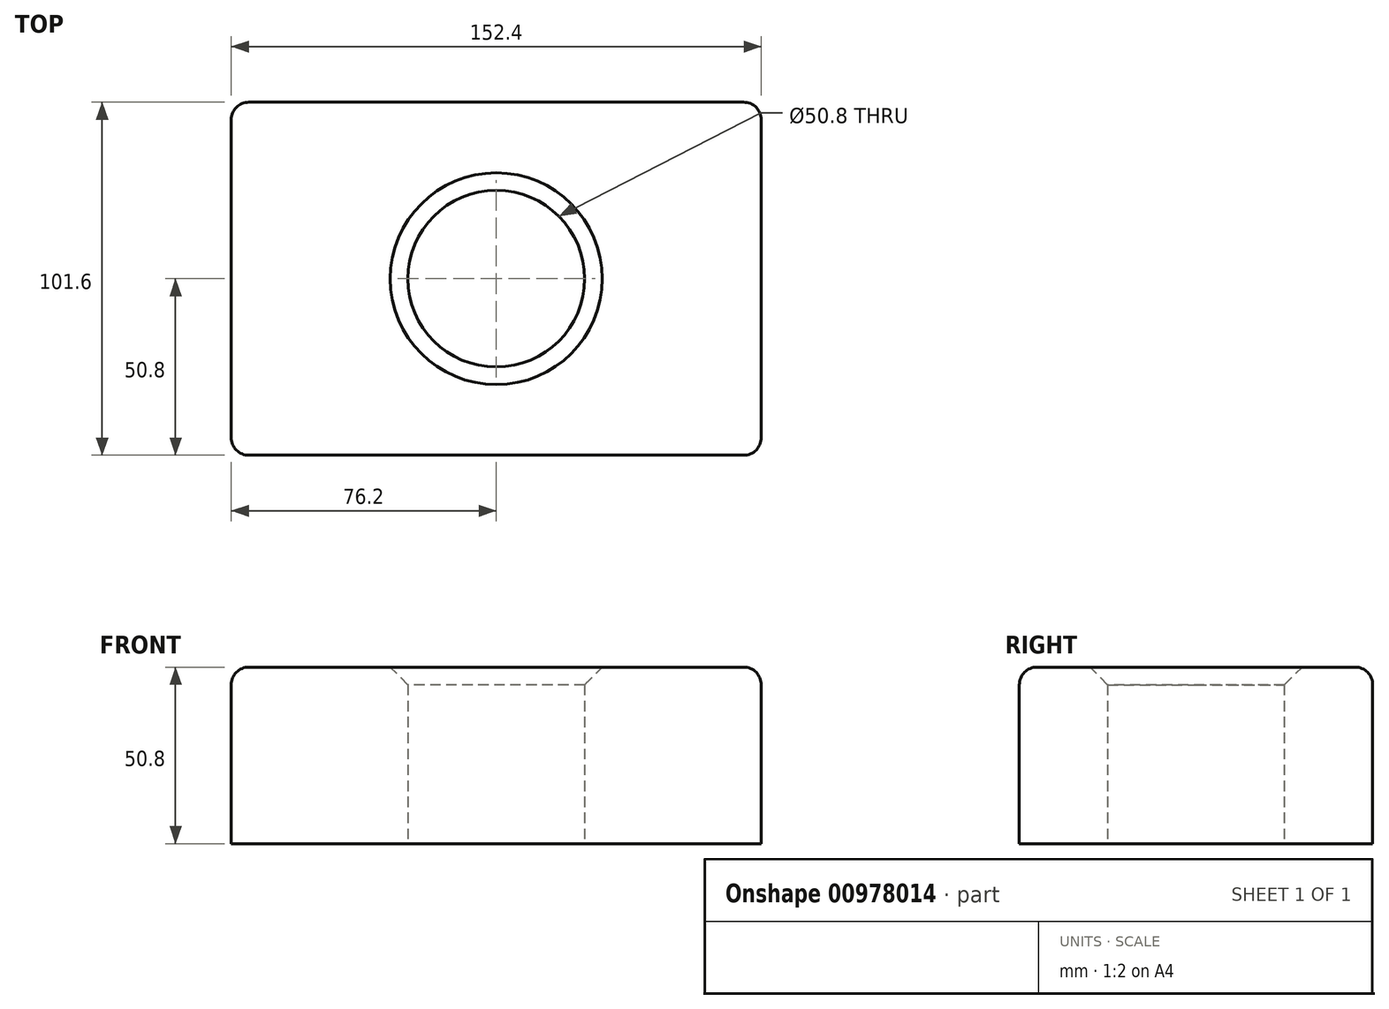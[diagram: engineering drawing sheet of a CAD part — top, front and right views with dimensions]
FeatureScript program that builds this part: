
annotation { "Feature Type Name" : "Feature", "Feature Type Description" : "" }
export const myFeature = defineFeature(function(context is Context, id is Id, definition is map)
    precondition{}
    {
        {
            var Q0;
            Q0=qCreatedBy(makeId("Top.planeOp"),FACE);
            var sketch = newSketch(context, id + "F0", { "sketchPlane" : qUnion([Q0])});
            skLineSegment(sketch, "E0.bottom", {"start": v(-76.2, 50.8) * mm, "end": v(76.2, 50.8) * mm});
            skLineSegment(sketch, "E0.top", {"start": v(-76.2, -50.8) * mm, "end": v(76.2, -50.8) * mm});
            skLineSegment(sketch, "E0.left", {"start": v(-76.2, 50.8) * mm, "end": v(-76.2, -50.8) * mm});
            skLineSegment(sketch, "E0.right", {"start": v(76.2, 50.8) * mm, "end": v(76.2, -50.8) * mm});
            skPoint(sketch, "E0.middle", {"position": v(0, 0) * mm});
            skCircle(sketch, "E1", {"center": v(0, 0) * mm, "radius": 25.4 * mm});
            skSolve(sketch);
        }
        {
            var Q0;
            Q0=makeQuery(id+"F0.imprint","IMPRINT",FACE,{"disambiguationData":[TD([[makeQuery(id+"F0.imprint","IMPRINT",EDGE,{"derivedFrom":sQuery(id+"F0.wireOp",EDGE,"E0.bottom")}),-1.0]])]});
            extrude(context, id + "F1", {"entities" : qUnion([Q0]), "depth" : 50.8 * mm, "offsetDistance" : 25.4 * mm});
        }
        {
            var Q0;
            Q0=makeQuery(id+"F1.opExtrude","CAP_EDGE",EDGE,{"disambiguationData":[OSD([sQuery(id+"F0.wireOp",EDGE,"E0.top")])],"isStart":false});
            fillet(context, id + "F2", {"entities" : qUnion([Q0]), "radius" : 5.08 * mm, "tangentPropagation" : true, "allowEdgeOverflow" : false});
        }
        {
            var Q0;
            Q0=makeQuery(id+"F1.opExtrude","CAP_EDGE",EDGE,{"disambiguationData":[OSD([sQuery(id+"F0.wireOp",EDGE,"E0.right")])],"isStart":false});
            fillet(context, id + "F3", {"entities" : qUnion([Q0]), "radius" : 5.08 * mm, "tangentPropagation" : true, "allowEdgeOverflow" : false});
        }
        {
            var Q0;
            Q0=makeQuery(id+"F1.opExtrude","CAP_EDGE",EDGE,{"disambiguationData":[OSD([sQuery(id+"F0.wireOp",EDGE,"E0.left")])],"isStart":false});
            fillet(context, id + "F4", {"entities" : qUnion([Q0]), "radius" : 5.08 * mm, "tangentPropagation" : true, "allowEdgeOverflow" : false});
        }
        {
            var Q0;
            {var subQ0=sQuery(id+"F0.wireOp",EDGE,"E0.left");Q0=makeQuery(id+"F4.opFillet","BLEND_EDGE",EDGE,{"blendedFrom":[makeQuery(id+"F1.opExtrude","CAP_EDGE",EDGE,{"disambiguationData":[OSD([subQ0])],"isStart":false}),makeQuery(id+"F1.opExtrude","CAP_FACE",FACE,{"disambiguationData":[OSD([sQuery(id+"F0.wireOp",EDGE,"E0.bottom"),sQuery(id+"F0.wireOp",EDGE,"E0.top"),subQ0,sQuery(id+"F0.wireOp",EDGE,"E0.right"),sQuery(id+"F0.wireOp",EDGE,"E1")])],"isStart":false})],"blendedInto":[makeQuery(id+"F1.opExtrude","CAP_FACE",FACE,{"disambiguationData":[OSD([sQuery(id+"F0.wireOp",EDGE,"E0.bottom"),sQuery(id+"F0.wireOp",EDGE,"E0.top"),subQ0,sQuery(id+"F0.wireOp",EDGE,"E0.right"),sQuery(id+"F0.wireOp",EDGE,"E1")])],"isStart":false})]});}
            var Q1;
            Q1=makeQuery(id+"F1.opExtrude","CAP_EDGE",EDGE,{"disambiguationData":[OSD([sQuery(id+"F0.wireOp",EDGE,"E0.bottom")])],"isStart":false});
            fillet(context, id + "F5", {"entities" : qUnion([Q0, Q1]), "radius" : 5.08 * mm, "tangentPropagation" : true, "allowEdgeOverflow" : false});
        }
        {
            var Q0;
            Q0=makeQuery(id+"F1.opExtrude","CAP_EDGE",EDGE,{"disambiguationData":[OSD([sQuery(id+"F0.wireOp",EDGE,"E1")])],"isStart":false});
            chamfer(context, id + "F6", {"entities" : qUnion([Q0]), "width" : 5.08 * mm, "tangentPropagation" : true});
        }
    });
